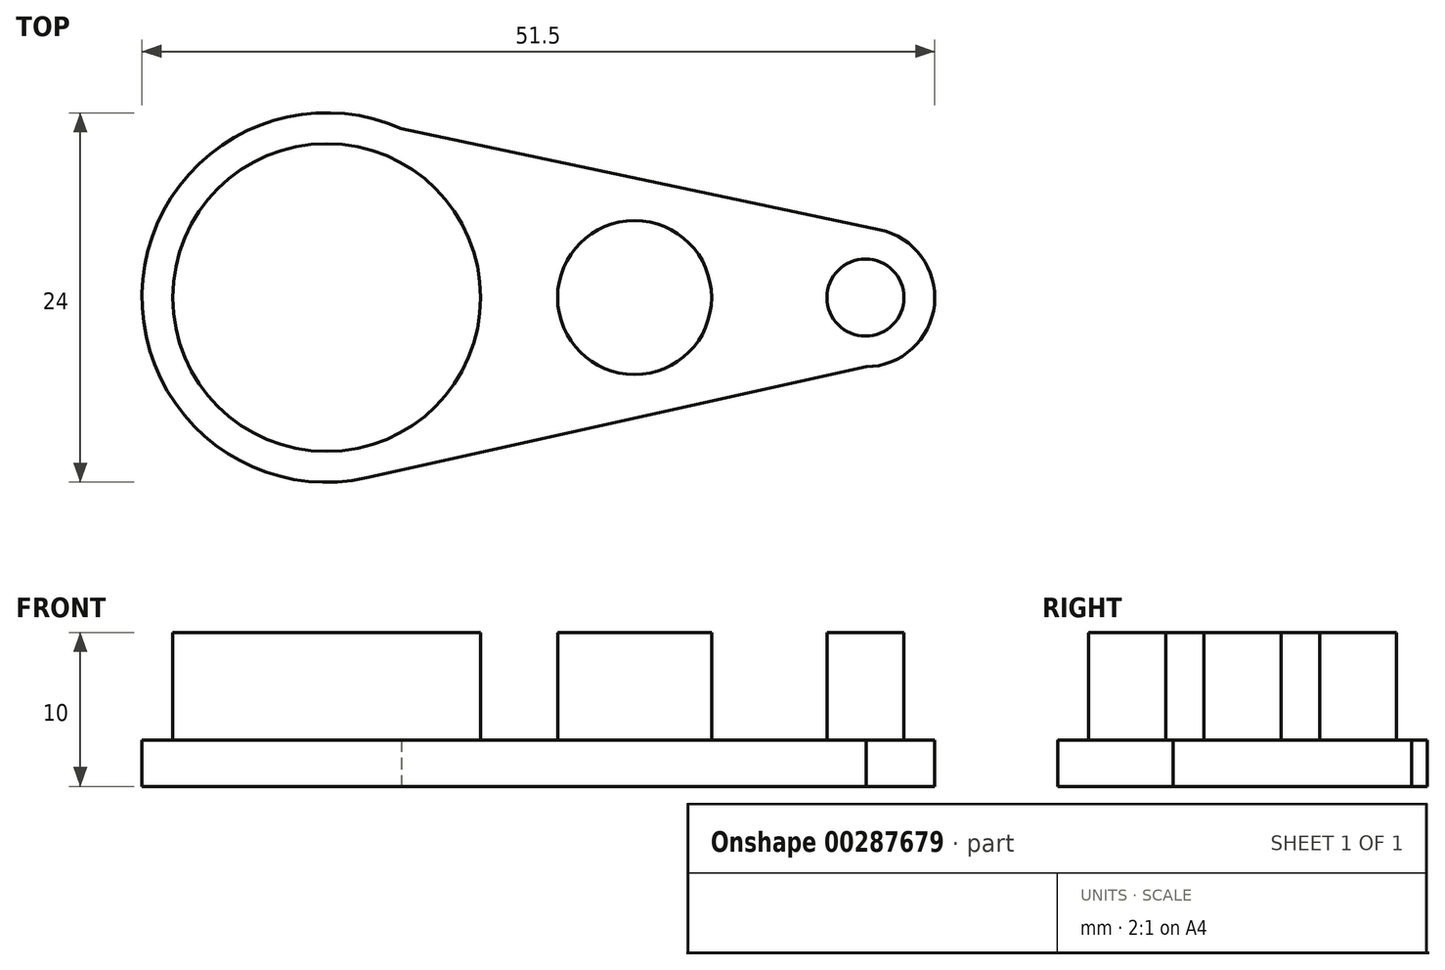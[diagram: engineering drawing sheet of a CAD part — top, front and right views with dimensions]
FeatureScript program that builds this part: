
annotation { "Feature Type Name" : "Feature", "Feature Type Description" : "" }
export const myFeature = defineFeature(function(context is Context, id is Id, definition is map)
    precondition{}
    {
        {
            var Q0;
            Q0=qCreatedBy(makeId("Top.planeOp"),FACE);
            var sketch = newSketch(context, id + "F0", { "sketchPlane" : qUnion([Q0])});
            skCircle(sketch, "E0", {"center": v(0, 0) * mm, "radius": 10 * mm});
            skCircle(sketch, "E1", {"center": v(20, 0) * mm, "radius": 5 * mm});
            skCircle(sketch, "E2", {"center": v(35, 0) * mm, "radius": 2.5 * mm});
            skArc(sketch, "E3.0", {"start": v(35.04, -4.5) * mm, "mid": v(39.48, -0.45) * mm, "end": v(35.93, 4.4) * mm});
            skArc(sketch, "E4.0", {"start": v(4.86, 10.97) * mm, "mid": v(-11.94, 1.19) * mm, "end": v(2.6, -11.71) * mm});
            skLineSegment(sketch, "E5", {"start": v(4.86, 10.97) * mm, "end": v(35.93, 4.4) * mm});
            skLineSegment(sketch, "E6", {"start": v(35.04, -4.5) * mm, "end": v(2.6, -11.71) * mm});
            skPoint(sketch, "E7.orphan", {"position": v(0, -12.3) * mm});
            skPoint(sketch, "E8.orphan", {"position": v(0, 12) * mm});
            skSolve(sketch);
        }
        {
            var Q0;
            Q0=qSketchRegion(id+"F0",true);
            var Q1;
            Q1=makeQuery(id+"F0.imprint","IMPRINT",FACE,{"disambiguationData":[TD([[makeQuery(id+"F0.imprint","IMPRINT",EDGE,{"derivedFrom":sQuery(id+"F0.wireOp",EDGE,"E0")}),1.0]])]});
            var Q2;
            Q2=makeQuery(id+"F0.imprint","IMPRINT",FACE,{"disambiguationData":[TD([[makeQuery(id+"F0.imprint","IMPRINT",EDGE,{"derivedFrom":sQuery(id+"F0.wireOp",EDGE,"E1")}),1.0]])]});
            var Q3;
            Q3=makeQuery(id+"F0.imprint","IMPRINT",FACE,{"disambiguationData":[TD([[makeQuery(id+"F0.imprint","IMPRINT",EDGE,{"derivedFrom":sQuery(id+"F0.wireOp",EDGE,"E2")}),1.0]])]});
            extrude(context, id + "F1", {"entities" : qUnion([Q0, Q1, Q2, Q3]), "depth" : 3 * mm});
        }
        {
            var Q0;
            Q0=makeQuery(id+"F0.imprint","IMPRINT",FACE,{"disambiguationData":[TD([[makeQuery(id+"F0.imprint","IMPRINT",EDGE,{"derivedFrom":sQuery(id+"F0.wireOp",EDGE,"E0")}),1.0]])]});
            var Q1;
            Q1=makeQuery(id+"F0.imprint","IMPRINT",FACE,{"disambiguationData":[TD([[makeQuery(id+"F0.imprint","IMPRINT",EDGE,{"derivedFrom":sQuery(id+"F0.wireOp",EDGE,"E1")}),1.0]])]});
            var Q2;
            Q2=makeQuery(id+"F0.imprint","IMPRINT",FACE,{"disambiguationData":[TD([[makeQuery(id+"F0.imprint","IMPRINT",EDGE,{"derivedFrom":sQuery(id+"F0.wireOp",EDGE,"E2")}),1.0]])]});
            extrude(context, id + "F2", {"entities" : qUnion([Q0, Q1, Q2]), "operationType" : NewBodyOperationType.ADD, "depth" : 10 * mm});
        }
    });
